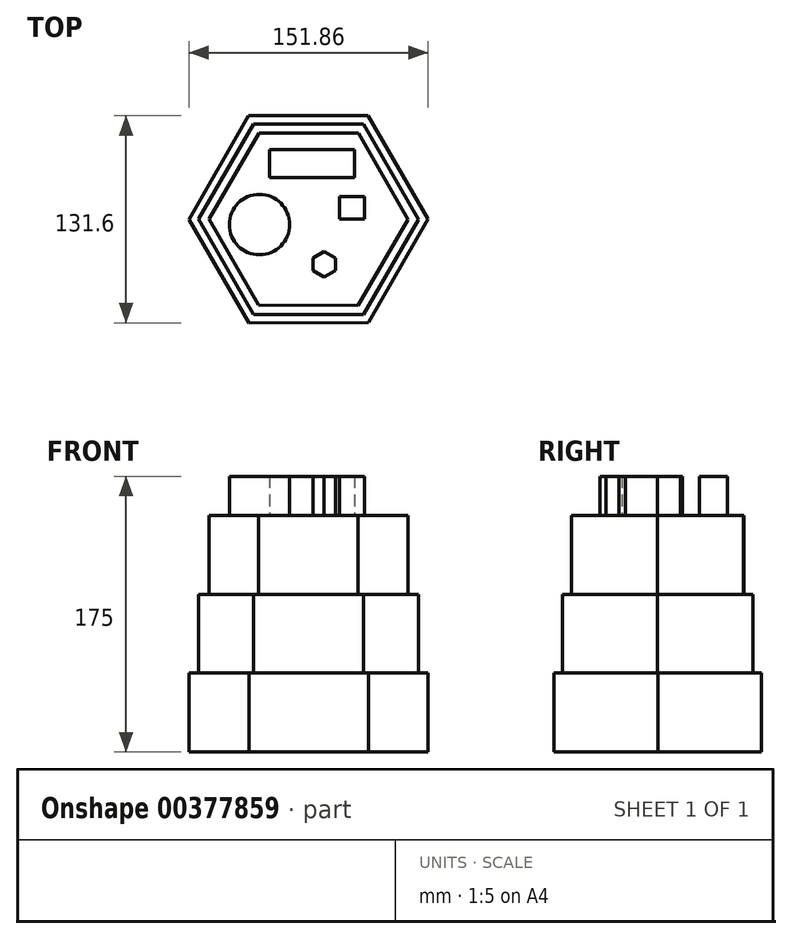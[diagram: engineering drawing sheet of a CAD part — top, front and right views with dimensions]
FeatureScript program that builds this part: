
annotation { "Feature Type Name" : "Feature", "Feature Type Description" : "" }
export const myFeature = defineFeature(function(context is Context, id is Id, definition is map)
    precondition{}
    {
        {
            var Q0;
            Q0=qCreatedBy(makeId("Top.planeOp"),FACE);
            var sketch = newSketch(context, id + "F0", { "sketchPlane" : qUnion([Q0])});
            skCircle(sketch, "E0.cCircle", {"center": v(0, 0) * mm, "radius": 65.76 * mm, "construction": true});
            skLineSegment(sketch, "E0.0", {"start": v(-75.93, -0.1) * mm, "end": v(-38.04, 65.71) * mm});
            skLineSegment(sketch, "E0.1", {"start": v(-38.04, 65.71) * mm, "end": v(37.89, 65.8) * mm});
            skLineSegment(sketch, "E0.2", {"start": v(37.89, 65.8) * mm, "end": v(75.93, 0.1) * mm});
            skLineSegment(sketch, "E0.3", {"start": v(75.93, 0.1) * mm, "end": v(38.04, -65.71) * mm});
            skLineSegment(sketch, "E0.4", {"start": v(38.04, -65.71) * mm, "end": v(-37.89, -65.8) * mm});
            skLineSegment(sketch, "E0.5", {"start": v(-37.89, -65.8) * mm, "end": v(-75.93, -0.1) * mm});
            skPoint(sketch, "E0.0.midPoint", {"position": v(-56.99, 32.8) * mm});
            skSolve(sketch);
        }
        {
            var Q0;
            Q0=makeQuery(id+"F0.imprint","IMPRINT",FACE,{"disambiguationData":[TD([[makeQuery(id+"F0.imprint","IMPRINT",EDGE,{"derivedFrom":sQuery(id+"F0.wireOp",EDGE,"E0.0")}),-1.0]])]});
            extrude(context, id + "F1", {"entities" : qUnion([Q0]), "depth" : 50 * mm});
        }
        {
            var Q0;
            Q0=makeQuery(id+"F1.opExtrude","CAP_FACE",FACE,{"disambiguationData":[OSD([sQuery(id+"F0.wireOp",EDGE,"E0.0"),sQuery(id+"F0.wireOp",EDGE,"E0.1"),sQuery(id+"F0.wireOp",EDGE,"E0.2"),sQuery(id+"F0.wireOp",EDGE,"E0.3"),sQuery(id+"F0.wireOp",EDGE,"E0.4"),sQuery(id+"F0.wireOp",EDGE,"E0.5")])],"isStart":false});
            var sketch = newSketch(context, id + "F2", { "sketchPlane" : qUnion([Q0])});
            skCircle(sketch, "E1.cCircle", {"center": v(0, 0) * mm, "radius": 60.54 * mm, "construction": true});
            skLineSegment(sketch, "E1.0", {"start": v(-69.9, 0.05) * mm, "end": v(-34.9, 60.57) * mm});
            skLineSegment(sketch, "E1.1", {"start": v(-34.9, 60.57) * mm, "end": v(35, 60.51) * mm});
            skLineSegment(sketch, "E1.2", {"start": v(35, 60.51) * mm, "end": v(69.9, -0.05) * mm});
            skLineSegment(sketch, "E1.3", {"start": v(69.9, -0.05) * mm, "end": v(34.9, -60.57) * mm});
            skLineSegment(sketch, "E1.4", {"start": v(34.9, -60.57) * mm, "end": v(-35, -60.51) * mm});
            skLineSegment(sketch, "E1.5", {"start": v(-35, -60.51) * mm, "end": v(-69.9, 0.05) * mm});
            skPoint(sketch, "E1.0.midPoint", {"position": v(-52.4, 30.31) * mm});
            skSolve(sketch);
        }
        {
            var Q0;
            Q0=makeQuery(id+"F2.imprint","IMPRINT",FACE,{"disambiguationData":[TD([[makeQuery(id+"F2.imprint","IMPRINT",EDGE,{"derivedFrom":sQuery(id+"F2.wireOp",EDGE,"E1.0")}),-1.0]])]});
            extrude(context, id + "F3", {"entities" : qUnion([Q0]), "operationType" : NewBodyOperationType.ADD, "depth" : 50 * mm});
        }
        {
            var Q0;
            Q0=makeQuery(id+"F3.opExtrude","CAP_FACE",FACE,{"disambiguationData":[OSD([sQuery(id+"F2.wireOp",EDGE,"E1.0"),sQuery(id+"F2.wireOp",EDGE,"E1.1"),sQuery(id+"F2.wireOp",EDGE,"E1.2"),sQuery(id+"F2.wireOp",EDGE,"E1.3"),sQuery(id+"F2.wireOp",EDGE,"E1.4"),sQuery(id+"F2.wireOp",EDGE,"E1.5")])],"isStart":false});
            var sketch = newSketch(context, id + "F4", { "sketchPlane" : qUnion([Q0])});
            skCircle(sketch, "E2.cCircle", {"center": v(0, 0) * mm, "radius": 54.7 * mm, "construction": true});
            skLineSegment(sketch, "E2.0", {"start": v(-63.17, 0.17) * mm, "end": v(-31.44, 54.8) * mm});
            skLineSegment(sketch, "E2.1", {"start": v(-31.44, 54.8) * mm, "end": v(31.73, 54.63) * mm});
            skLineSegment(sketch, "E2.2", {"start": v(31.73, 54.63) * mm, "end": v(63.17, -0.17) * mm});
            skLineSegment(sketch, "E2.3", {"start": v(63.17, -0.17) * mm, "end": v(31.44, -54.8) * mm});
            skLineSegment(sketch, "E2.4", {"start": v(31.44, -54.8) * mm, "end": v(-31.73, -54.63) * mm});
            skLineSegment(sketch, "E2.5", {"start": v(-31.73, -54.63) * mm, "end": v(-63.17, 0.17) * mm});
            skPoint(sketch, "E2.0.midPoint", {"position": v(-47.3, 27.48) * mm});
            skSolve(sketch);
        }
        {
            var Q0;
            Q0=makeQuery(id+"F4.imprint","IMPRINT",FACE,{"disambiguationData":[TD([[makeQuery(id+"F4.imprint","IMPRINT",EDGE,{"derivedFrom":sQuery(id+"F4.wireOp",EDGE,"E2.0")}),-1.0]])]});
            extrude(context, id + "F5", {"entities" : qUnion([Q0]), "operationType" : NewBodyOperationType.ADD, "depth" : 50 * mm});
        }
        {
            var Q0;
            Q0=makeQuery(id+"F5.opExtrude","CAP_FACE",FACE,{"disambiguationData":[OSD([sQuery(id+"F4.wireOp",EDGE,"E2.0"),sQuery(id+"F4.wireOp",EDGE,"E2.1"),sQuery(id+"F4.wireOp",EDGE,"E2.2"),sQuery(id+"F4.wireOp",EDGE,"E2.3"),sQuery(id+"F4.wireOp",EDGE,"E2.4"),sQuery(id+"F4.wireOp",EDGE,"E2.5")])],"isStart":false});
            var sketch = newSketch(context, id + "F6", { "sketchPlane" : qUnion([Q0])});
            skLineSegment(sketch, "E3.bottom", {"start": v(-24.93, 44.2) * mm, "end": v(29.18, 44.2) * mm});
            skLineSegment(sketch, "E3.top", {"start": v(-24.93, 26.63) * mm, "end": v(29.18, 26.63) * mm});
            skLineSegment(sketch, "E3.left", {"start": v(-24.93, 44.2) * mm, "end": v(-24.93, 26.63) * mm});
            skLineSegment(sketch, "E3.right", {"start": v(29.18, 44.2) * mm, "end": v(29.18, 26.63) * mm});
            skLineSegment(sketch, "E4.bottom", {"start": v(19.83, 14.45) * mm, "end": v(35.4, 14.45) * mm});
            skLineSegment(sketch, "E4.top", {"start": v(19.83, 0) * mm, "end": v(35.4, 0) * mm});
            skLineSegment(sketch, "E4.left", {"start": v(19.83, 14.45) * mm, "end": v(19.83, 0) * mm});
            skLineSegment(sketch, "E4.right", {"start": v(35.4, 14.45) * mm, "end": v(35.4, 0) * mm});
            skCircle(sketch, "E5", {"center": v(-31.16, -3.4) * mm, "radius": 19.17 * mm});
            skCircle(sketch, "E6.cCircle", {"center": v(9.91, -28.61) * mm, "radius": 7.08 * mm, "construction": true});
            skLineSegment(sketch, "E6.0", {"start": v(2.83, -32.7) * mm, "end": v(2.83, -24.52) * mm});
            skLineSegment(sketch, "E6.1", {"start": v(2.83, -24.52) * mm, "end": v(9.91, -20.43) * mm});
            skLineSegment(sketch, "E6.2", {"start": v(9.91, -20.43) * mm, "end": v(17, -24.52) * mm});
            skLineSegment(sketch, "E6.3", {"start": v(17, -24.52) * mm, "end": v(17, -32.7) * mm});
            skLineSegment(sketch, "E6.4", {"start": v(17, -32.7) * mm, "end": v(9.91, -36.79) * mm});
            skLineSegment(sketch, "E6.5", {"start": v(9.91, -36.79) * mm, "end": v(2.83, -32.7) * mm});
            skPoint(sketch, "E6.0.midPoint", {"position": v(2.83, -28.61) * mm});
            skSolve(sketch);
        }
        {
            var Q0;
            Q0=makeQuery(id+"F6.imprint","IMPRINT",FACE,{"disambiguationData":[TD([[makeQuery(id+"F6.imprint","IMPRINT",EDGE,{"derivedFrom":sQuery(id+"F6.wireOp",EDGE,"E3.bottom")}),-1.0]])]});
            var Q1;
            Q1=makeQuery(id+"F6.imprint","IMPRINT",FACE,{"disambiguationData":[TD([[makeQuery(id+"F6.imprint","IMPRINT",EDGE,{"derivedFrom":sQuery(id+"F6.wireOp",EDGE,"E5")}),1.0]])]});
            var Q2;
            Q2=makeQuery(id+"F6.imprint","IMPRINT",FACE,{"disambiguationData":[TD([[makeQuery(id+"F6.imprint","IMPRINT",EDGE,{"derivedFrom":sQuery(id+"F6.wireOp",EDGE,"E4.bottom")}),-1.0]])]});
            var Q3;
            Q3=makeQuery(id+"F6.imprint","IMPRINT",FACE,{"disambiguationData":[TD([[makeQuery(id+"F6.imprint","IMPRINT",EDGE,{"derivedFrom":sQuery(id+"F6.wireOp",EDGE,"E6.0")}),-1.0]])]});
            extrude(context, id + "F7", {"entities" : qUnion([Q0, Q1, Q2, Q3]), "operationType" : NewBodyOperationType.ADD, "depth" : 25 * mm});
        }
    });
